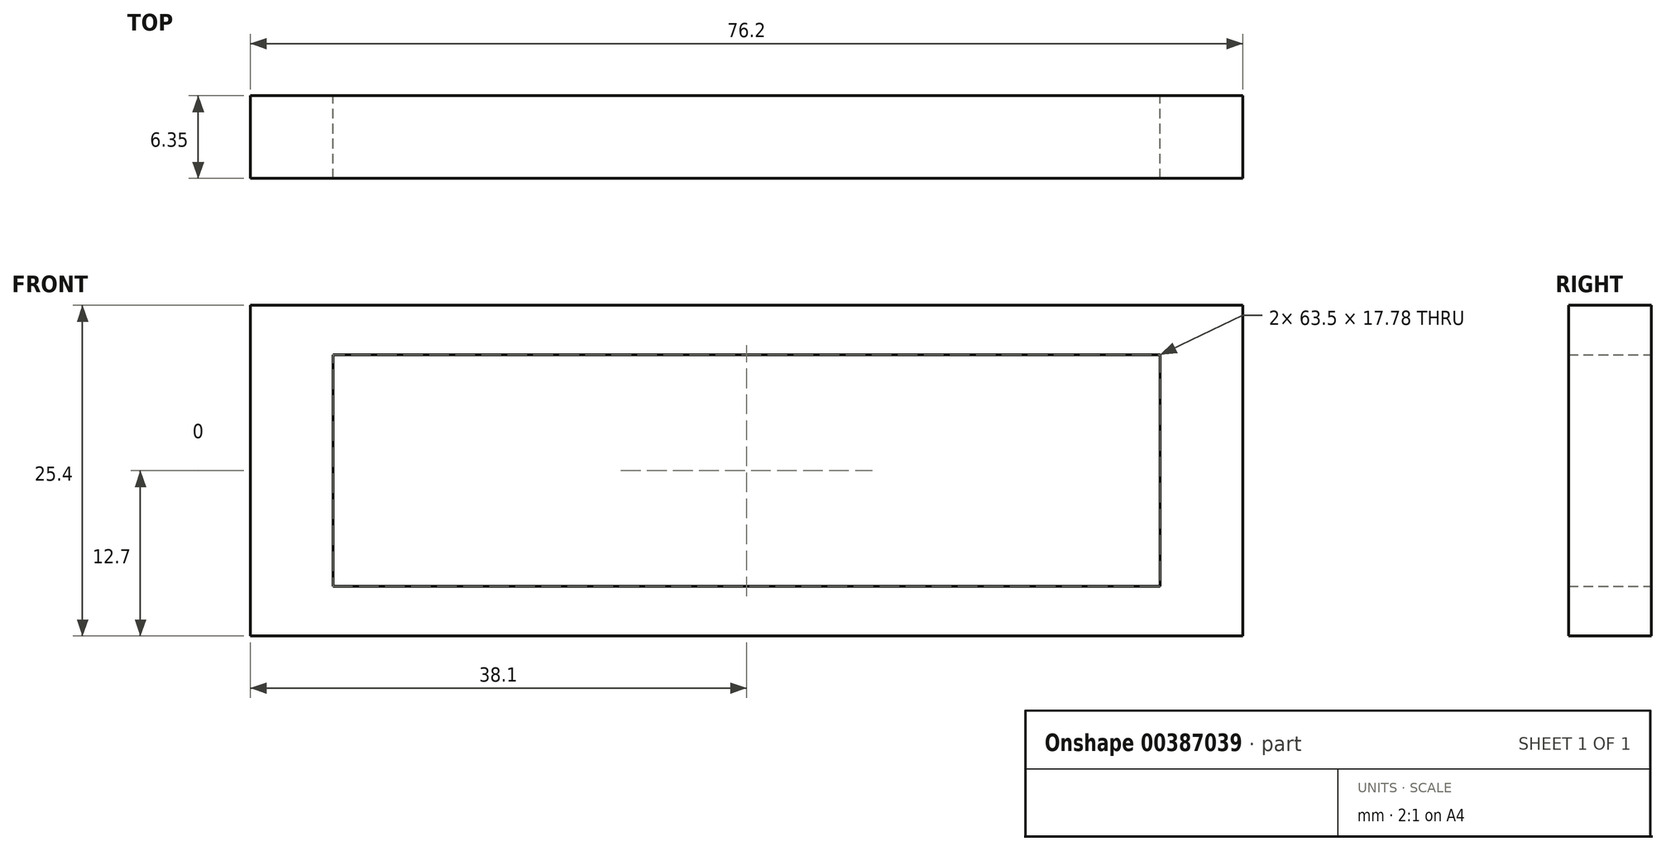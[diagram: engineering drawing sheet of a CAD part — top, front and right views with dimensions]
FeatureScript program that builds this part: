
annotation { "Feature Type Name" : "Feature", "Feature Type Description" : "" }
export const myFeature = defineFeature(function(context is Context, id is Id, definition is map)
    precondition{}
    {
        {
            var Q0;
            Q0=qCreatedBy(makeId("Front.planeOp"),FACE);
            var sketch = newSketch(context, id + "F0", { "sketchPlane" : qUnion([Q0])});
            skLineSegment(sketch, "E0.bottom", {"start": v(38.1, -12.7) * mm, "end": v(-38.1, -12.7) * mm});
            skLineSegment(sketch, "E0.top", {"start": v(38.1, 12.7) * mm, "end": v(-38.1, 12.7) * mm});
            skLineSegment(sketch, "E0.left", {"start": v(38.1, -12.7) * mm, "end": v(38.1, 12.7) * mm});
            skLineSegment(sketch, "E0.right", {"start": v(-38.1, -12.7) * mm, "end": v(-38.1, 12.7) * mm});
            skPoint(sketch, "E0.middle", {"position": v(0, 0) * mm});
            skLineSegment(sketch, "E1.bottom", {"start": v(31.75, -8.89) * mm, "end": v(-31.75, -8.9) * mm});
            skLineSegment(sketch, "E1.top", {"start": v(31.75, 8.9) * mm, "end": v(-31.75, 8.89) * mm});
            skLineSegment(sketch, "E1.left", {"start": v(31.75, -8.89) * mm, "end": v(31.75, 8.9) * mm});
            skLineSegment(sketch, "E1.right", {"start": v(-31.75, -8.9) * mm, "end": v(-31.75, 8.89) * mm});
            skSolve(sketch);
        }
        {
            var Q0;
            Q0=makeQuery(id+"F0.imprint","IMPRINT",FACE,{"disambiguationData":[TD([[makeQuery(id+"F0.imprint","IMPRINT",EDGE,{"derivedFrom":sQuery(id+"F0.wireOp",EDGE,"E0.bottom")}),-1.0]])]});
            extrude(context, id + "F1", {"entities" : qUnion([Q0]), "depth" : 6.35 * mm});
        }
    });
